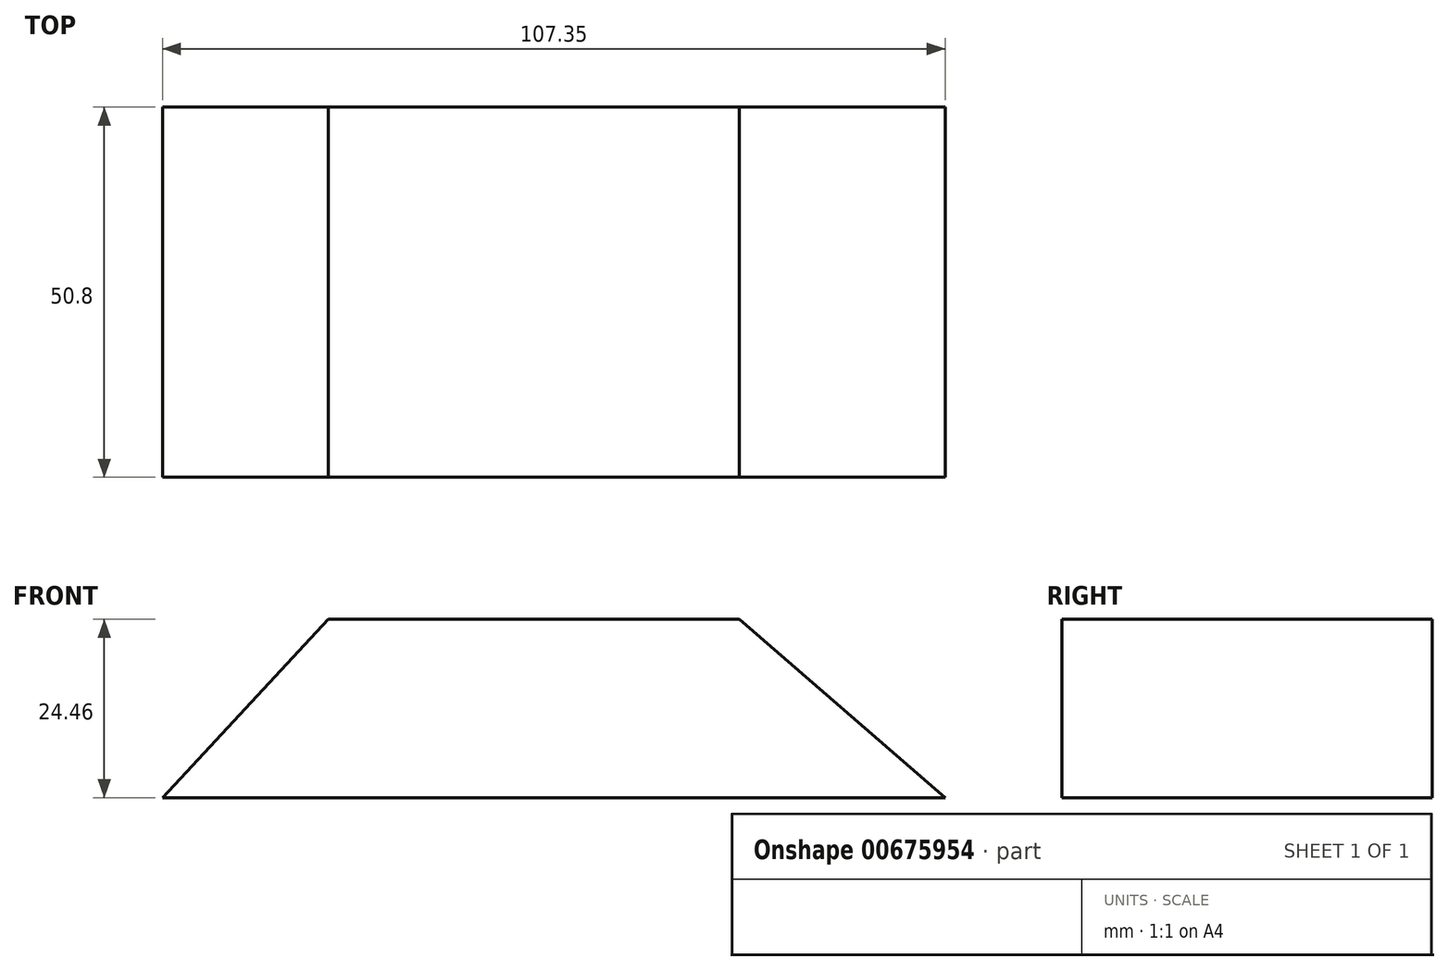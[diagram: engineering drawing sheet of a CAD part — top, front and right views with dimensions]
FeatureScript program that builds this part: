
annotation { "Feature Type Name" : "Feature", "Feature Type Description" : "" }
export const myFeature = defineFeature(function(context is Context, id is Id, definition is map)
    precondition{}
    {
        {
            var Q0;
            Q0=qCreatedBy(makeId("Front.planeOp"),FACE);
            var sketch = newSketch(context, id + "F0", { "sketchPlane" : qUnion([Q0])});
            skLineSegment(sketch, "E0", {"start": v(-50.8, -28.06) * mm, "end": v(56.55, -28.06) * mm});
            skLineSegment(sketch, "E1", {"start": v(56.55, -28.06) * mm, "end": v(28.35, -3.6) * mm});
            skLineSegment(sketch, "E2", {"start": v(28.35, -3.6) * mm, "end": v(-28.06, -3.6) * mm});
            skLineSegment(sketch, "E3", {"start": v(-50.8, -28.06) * mm, "end": v(-28.06, -3.6) * mm});
            skSolve(sketch);
        }
        {
            var Q0;
            Q0=makeQuery(id+"F0.imprint","IMPRINT",FACE,{"disambiguationData":[TD([[makeQuery(id+"F0.imprint","IMPRINT",EDGE,{"derivedFrom":sQuery(id+"F0.wireOp",EDGE,"E0")}),1.0]])]});
            extrude(context, id + "F1", {"entities" : qUnion([Q0]), "depth" : 50.8 * mm, "offsetDistance" : 25.4 * mm});
        }
    });
